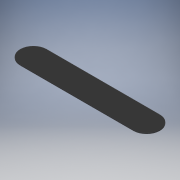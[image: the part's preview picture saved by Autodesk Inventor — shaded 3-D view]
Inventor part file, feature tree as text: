
AUTODESK INVENTOR PART (.ipt)
format: ipt  version: 2018 (Build 220112000, 112)  size: 94,720 bytes
history: native  units: mm
features: extrude x1, sketch x1
ambient origin geometry x8: Origin, YZ Plane, XZ Plane, XY Plane, X Axis, Y Axis, Z Axis, Center Point
bodies: Solid1 (feature_tree)
feature tree (2):
  extrude  "Extrusion1"  Depth=100.0mm
  sketch  "Sketch1"  dims[d2=530.0mm d3=100.0mm d4=3.0mm d5=0.0mm]
